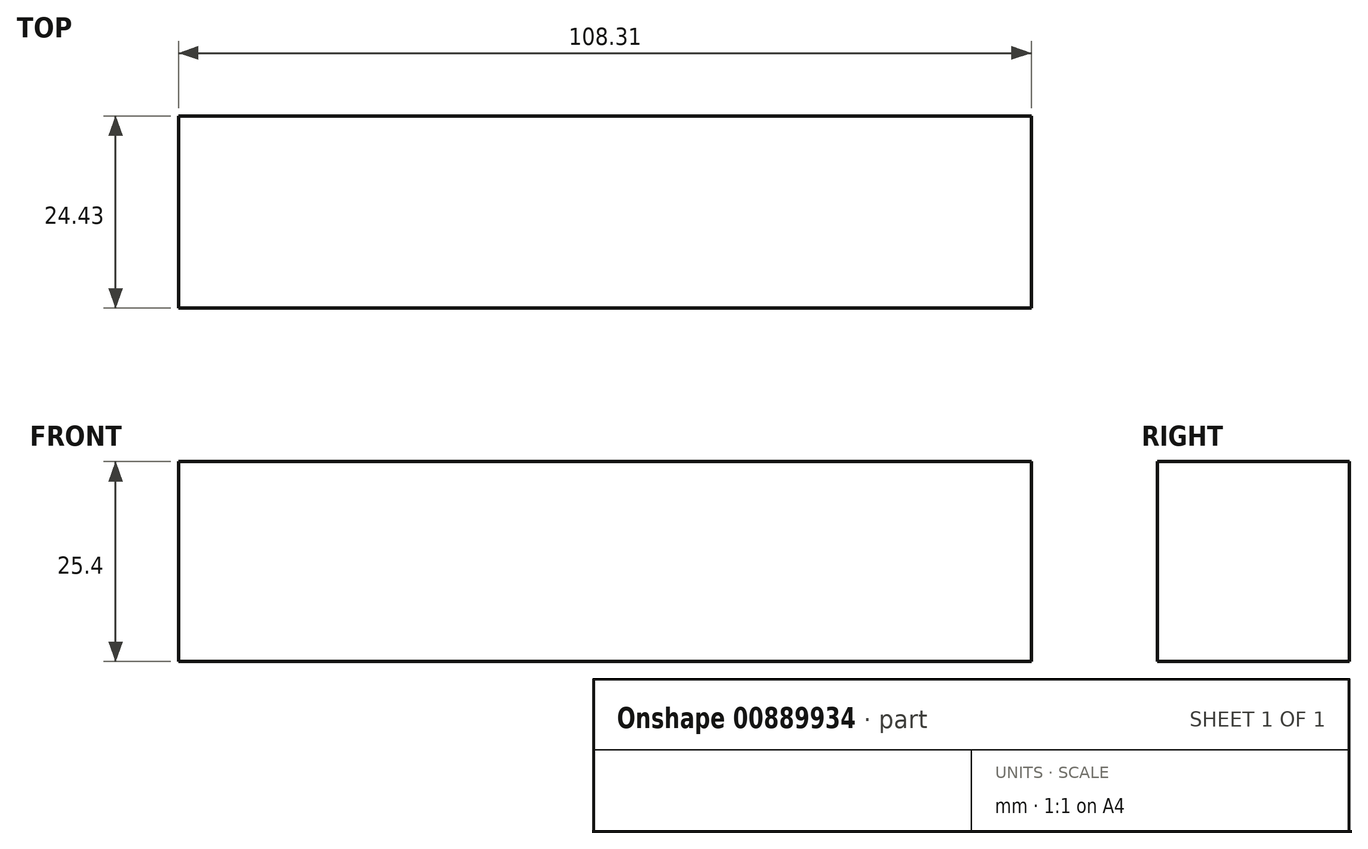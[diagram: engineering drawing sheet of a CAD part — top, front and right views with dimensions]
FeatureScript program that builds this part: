
annotation { "Feature Type Name" : "Feature", "Feature Type Description" : "" }
export const myFeature = defineFeature(function(context is Context, id is Id, definition is map)
    precondition{}
    {
        {
            var Q0;
            Q0=qCreatedBy(makeId("Top.planeOp"),FACE);
            var sketch = newSketch(context, id + "F0", { "sketchPlane" : qUnion([Q0])});
            skLineSegment(sketch, "E0.bottom", {"start": v(-67.64, -52.1) * mm, "end": v(40.67, -52.1) * mm});
            skLineSegment(sketch, "E0.top", {"start": v(-67.64, -27.66) * mm, "end": v(40.67, -27.66) * mm});
            skLineSegment(sketch, "E0.left", {"start": v(-67.64, -52.1) * mm, "end": v(-67.64, -27.66) * mm});
            skLineSegment(sketch, "E0.right", {"start": v(40.67, -52.1) * mm, "end": v(40.67, -27.66) * mm});
            skSolve(sketch);
        }
        {
            var Q0;
            Q0 = qSketchRegion(id + "F0", true);
            extrude(context, id + "F1", {"entities" : qUnion([Q0]), "depth" : 25.4 * mm, "offsetDistance" : 25.4 * mm});
        }
    });
